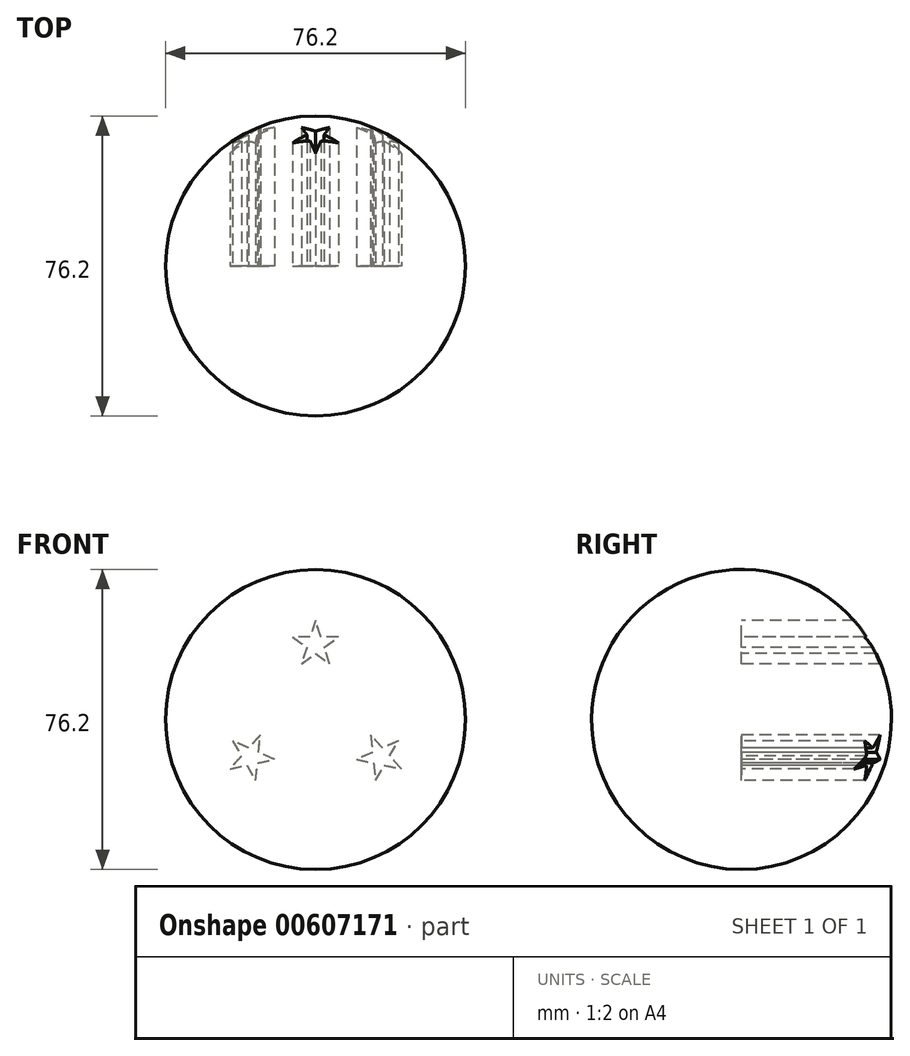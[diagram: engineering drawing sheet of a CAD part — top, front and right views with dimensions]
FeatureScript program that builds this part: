
annotation { "Feature Type Name" : "Feature", "Feature Type Description" : "" }
export const myFeature = defineFeature(function(context is Context, id is Id, definition is map)
    precondition{}
    {
        {
            var Q0;
            Q0=qCreatedBy(makeId("Top.planeOp"),FACE);
            var sketch = newSketch(context, id + "F0", { "sketchPlane" : qUnion([Q0])});
            skLineSegment(sketch, "E0", {"start": v(0, 0) * mm, "end": v(0, 38.1) * mm});
            skLineSegment(sketch, "E1", {"start": v(0, 0) * mm, "end": v(38.1, 0) * mm});
            skArc(sketch, "E2", {"start": v(38.1, 0) * mm, "mid": v(26.94, 26.94) * mm, "end": v(0, 38.1) * mm});
            skSolve(sketch);
        }
        {
            var Q0;
            Q0=makeQuery(id+"F0.imprint","IMPRINT",FACE,{"disambiguationData":[TD([[makeQuery(id+"F0.imprint","IMPRINT",EDGE,{"derivedFrom":sQuery(id+"F0.wireOp",EDGE,"E0")}),-1.0]])]});
            var Q1;
            Q1=sQuery(id+"F0.wireOp",EDGE,"E0");
            revolve(context, id + "F1", {"entities" : qUnion([Q0]), "axis" : qUnion([Q1]), "revolveType" : RevolveType.FULL});
        }
        {
            var Q0;
            Q0=makeQuery(id+"F1.opRevolve","SWEPT_FACE",FACE,{"disambiguationData":[OSD([sQuery(id+"F0.wireOp",EDGE,"E1")])]});
            var sketch = newSketch(context, id + "F2", { "sketchPlane" : qUnion([Q0])});
            skLineSegment(sketch, "E3", {"start": v(0, 0) * mm, "end": v(0, 38.1) * mm});
            skLineSegment(sketch, "E4.2", {"start": v(3.59, 14.11) * mm, "end": v(-3.59, 14.11) * mm});
            skLineSegment(sketch, "E5", {"start": v(0, 25.15) * mm, "end": v(-1.37, 20.94) * mm});
            skLineSegment(sketch, "E6", {"start": v(-1.37, 20.94) * mm, "end": v(-5.8, 20.94) * mm});
            skLineSegment(sketch, "E7", {"start": v(-5.8, 20.94) * mm, "end": v(-2.22, 18.33) * mm});
            skLineSegment(sketch, "E8", {"start": v(-2.22, 18.33) * mm, "end": v(-3.59, 14.11) * mm});
            skLineSegment(sketch, "E9", {"start": v(-3.59, 14.11) * mm, "end": v(0, 16.72) * mm});
            skLineSegment(sketch, "E10", {"start": v(0, 16.72) * mm, "end": v(3.59, 14.11) * mm});
            skLineSegment(sketch, "E11", {"start": v(3.59, 14.11) * mm, "end": v(2.22, 18.33) * mm});
            skLineSegment(sketch, "E12", {"start": v(2.22, 18.33) * mm, "end": v(5.8, 20.94) * mm});
            skLineSegment(sketch, "E13", {"start": v(5.8, 20.94) * mm, "end": v(1.37, 20.94) * mm});
            skLineSegment(sketch, "E14", {"start": v(1.37, 20.94) * mm, "end": v(0, 25.15) * mm});
            skLineSegment(sketch, "E15.1.0", {"start": v(-21.78, -12.58) * mm, "end": v(-17.45, -11.65) * mm});
            skLineSegment(sketch, "E15.1.1", {"start": v(-18.82, -9.28) * mm, "end": v(-21.78, -12.58) * mm});
            skLineSegment(sketch, "E15.1.2", {"start": v(-17.45, -11.65) * mm, "end": v(-15.23, -15.5) * mm});
            skLineSegment(sketch, "E15.1.3", {"start": v(-15.23, -15.5) * mm, "end": v(-14.77, -11.08) * mm});
            skLineSegment(sketch, "E15.1.4", {"start": v(-14.77, -11.08) * mm, "end": v(-10.43, -10.16) * mm});
            skLineSegment(sketch, "E15.1.5", {"start": v(-10.43, -10.16) * mm, "end": v(-14.48, -8.36) * mm});
            skLineSegment(sketch, "E15.1.6", {"start": v(-14.48, -8.36) * mm, "end": v(-14.02, -3.95) * mm});
            skLineSegment(sketch, "E15.1.7", {"start": v(-14.02, -3.95) * mm, "end": v(-16.98, -7.24) * mm});
            skLineSegment(sketch, "E15.1.8", {"start": v(-16.98, -7.24) * mm, "end": v(-21.03, -5.44) * mm});
            skLineSegment(sketch, "E15.1.9", {"start": v(-21.03, -5.44) * mm, "end": v(-18.82, -9.28) * mm});
            skLineSegment(sketch, "E15.2.0", {"start": v(21.78, -12.58) * mm, "end": v(18.82, -9.28) * mm});
            skLineSegment(sketch, "E15.2.1", {"start": v(17.45, -11.65) * mm, "end": v(21.78, -12.58) * mm});
            skLineSegment(sketch, "E15.2.2", {"start": v(18.82, -9.28) * mm, "end": v(21.03, -5.44) * mm});
            skLineSegment(sketch, "E15.2.3", {"start": v(21.03, -5.44) * mm, "end": v(16.98, -7.24) * mm});
            skLineSegment(sketch, "E15.2.4", {"start": v(16.98, -7.24) * mm, "end": v(14.02, -3.95) * mm});
            skLineSegment(sketch, "E15.2.5", {"start": v(14.02, -3.95) * mm, "end": v(14.48, -8.36) * mm});
            skLineSegment(sketch, "E15.2.6", {"start": v(14.48, -8.36) * mm, "end": v(10.43, -10.16) * mm});
            skLineSegment(sketch, "E15.2.7", {"start": v(10.43, -10.16) * mm, "end": v(14.77, -11.08) * mm});
            skLineSegment(sketch, "E15.2.8", {"start": v(14.77, -11.08) * mm, "end": v(15.23, -15.5) * mm});
            skLineSegment(sketch, "E15.2.9", {"start": v(15.23, -15.5) * mm, "end": v(17.45, -11.65) * mm});
            skPoint(sketch, "E15.center", {"position": v(0, 0) * mm});
            skSolve(sketch);
        }
        {
            var Q0;
            {var subQ0=sQuery(id+"F2.wireOp",EDGE,"E10");Q0=makeQuery(id+"F2.imprint","IMPRINT",FACE,{"disambiguationData":[TD([[makeQuery(id+"F2.imprint","IMPRINT",EDGE,{"derivedFrom":subQ0}),1.0]])]});}
            var Q1;
            {var subQ0=sQuery(id+"F2.wireOp",EDGE,"E5");Q1=makeQuery(id+"F2.imprint","IMPRINT",FACE,{"disambiguationData":[TD([[makeQuery(id+"F2.imprint","IMPRINT",EDGE,{"derivedFrom":subQ0}),1.0]])]});}
            var Q2;
            Q2=makeQuery(id+"F2.imprint","IMPRINT",FACE,{"disambiguationData":[TD([[makeQuery(id+"F2.imprint","IMPRINT",EDGE,{"derivedFrom":sQuery(id+"F2.wireOp",EDGE,"E15.1.0")}),1.0]])]});
            var Q3;
            Q3=makeQuery(id+"F2.imprint","IMPRINT",FACE,{"disambiguationData":[TD([[makeQuery(id+"F2.imprint","IMPRINT",EDGE,{"derivedFrom":sQuery(id+"F2.wireOp",EDGE,"E15.2.0")}),1.0]])]});
            extrude(context, id + "F3", {"entities" : qUnion([Q0, Q1, Q2, Q3]), "operationType" : NewBodyOperationType.REMOVE, "oppositeDirection" : true, "depth" : 50.8 * mm, "offsetDistance" : 25.4 * mm});
        }
        {
            var Q0;
            Q0=qCreatedBy(makeId("Top.planeOp"),FACE);
            var sketch = newSketch(context, id + "F4", { "sketchPlane" : qUnion([Q0])});
            skLineSegment(sketch, "E16", {"start": v(0, 0) * mm, "end": v(38.1, 0) * mm});
            skLineSegment(sketch, "E17", {"start": v(0, 0) * mm, "end": v(0, -38.1) * mm});
            skArc(sketch, "E18", {"start": v(0, -38.1) * mm, "mid": v(26.94, -26.94) * mm, "end": v(38.1, 0) * mm});
            skSolve(sketch);
        }
        {
            var Q0;
            Q0=makeQuery(id+"F4.imprint","IMPRINT",FACE,{"disambiguationData":[TD([[makeQuery(id+"F4.imprint","IMPRINT",EDGE,{"derivedFrom":sQuery(id+"F4.wireOp",EDGE,"E16")}),-1.0]])]});
            var Q1;
            Q1=sQuery(id+"F4.wireOp",EDGE,"E17");
            revolve(context, id + "F5", {"operationType" : NewBodyOperationType.ADD, "entities" : qUnion([Q0]), "axis" : qUnion([Q1]), "revolveType" : RevolveType.FULL});
        }
    });
